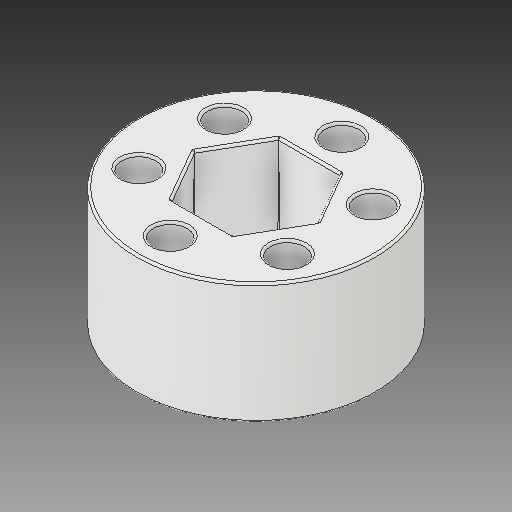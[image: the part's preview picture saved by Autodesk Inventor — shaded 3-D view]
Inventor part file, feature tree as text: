
AUTODESK INVENTOR PART (.ipt)
format: ipt  version: 2018 (Build 220112000, 112)  size: 248,832 bytes
history: native  units: in
note: dims shown in document units (in); Inventor stores cm internally (conversion verified against a paired STEP export)
features: fillet x1
ambient origin geometry x8: Origin, YZ Plane, XZ Plane, XY Plane, X Axis, Y Axis, Z Axis, Center Point
bodies: Solid1 (feature_tree)
feature tree (1):
  fillet  "Fillet2"  [1 undecoded]
note: 1 required parameter value undecoded (feature->parameter linkage not recoverable at this tier; creation-order binding heuristic only, values carry confidence <= 0.55)
